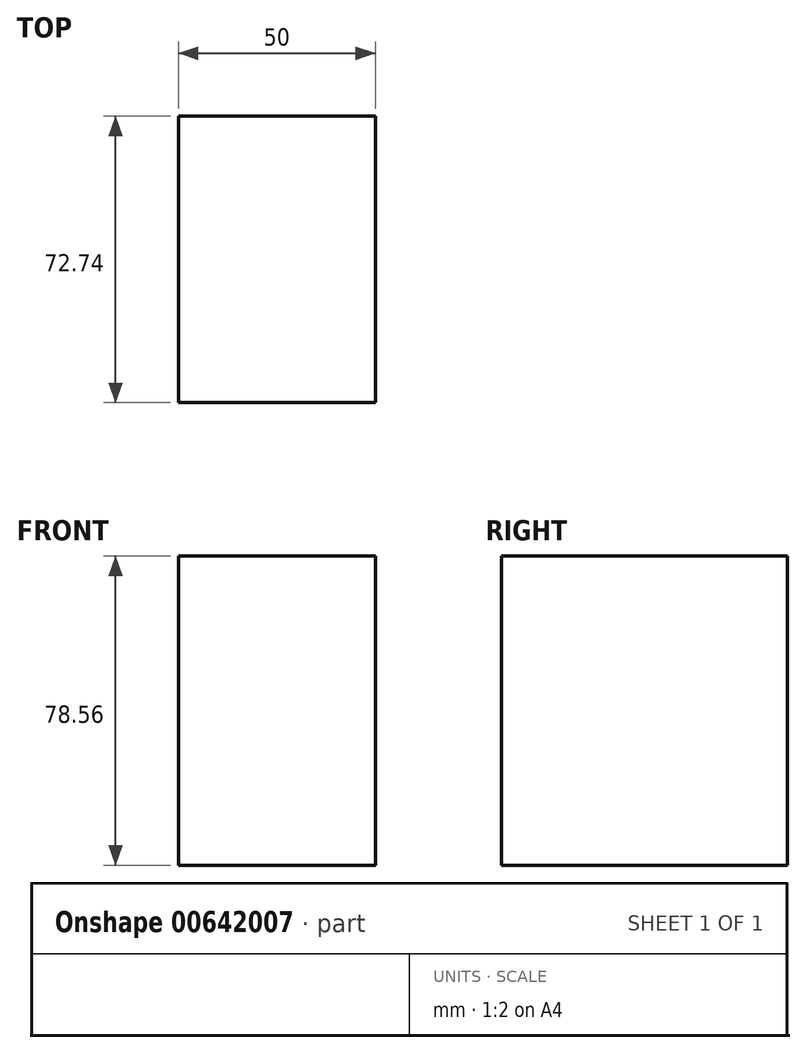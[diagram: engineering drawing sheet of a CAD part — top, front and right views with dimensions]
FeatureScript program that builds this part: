
annotation { "Feature Type Name" : "Feature", "Feature Type Description" : "" }
export const myFeature = defineFeature(function(context is Context, id is Id, definition is map)
    precondition{}
    {
        {
            var Q0;
            Q0=qCreatedBy(makeId("Right.planeOp"),FACE);
            var sketch = newSketch(context, id + "F0", { "sketchPlane" : qUnion([Q0])});
            skLineSegment(sketch, "E0.bottom", {"start": v(36.37, -39.28) * mm, "end": v(-36.37, -39.28) * mm});
            skLineSegment(sketch, "E0.top", {"start": v(36.37, 39.28) * mm, "end": v(-36.37, 39.28) * mm});
            skLineSegment(sketch, "E0.left", {"start": v(36.37, -39.28) * mm, "end": v(36.37, 39.28) * mm});
            skLineSegment(sketch, "E0.right", {"start": v(-36.37, -39.28) * mm, "end": v(-36.37, 39.28) * mm});
            skPoint(sketch, "E0.middle", {"position": v(0, 0) * mm});
            skSolve(sketch);
        }
        {
            var Q0;
            Q0=makeQuery(id+"F0.imprint","IMPRINT",FACE,{"disambiguationData":[TD([[makeQuery(id+"F0.imprint","IMPRINT",EDGE,{"derivedFrom":sQuery(id+"F0.wireOp",EDGE,"E0.bottom")}),-1.0]])]});
            extrude(context, id + "F1", {"entities" : qUnion([Q0]), "depth" : 50 * mm, "offsetDistance" : 25 * mm});
        }
    });
